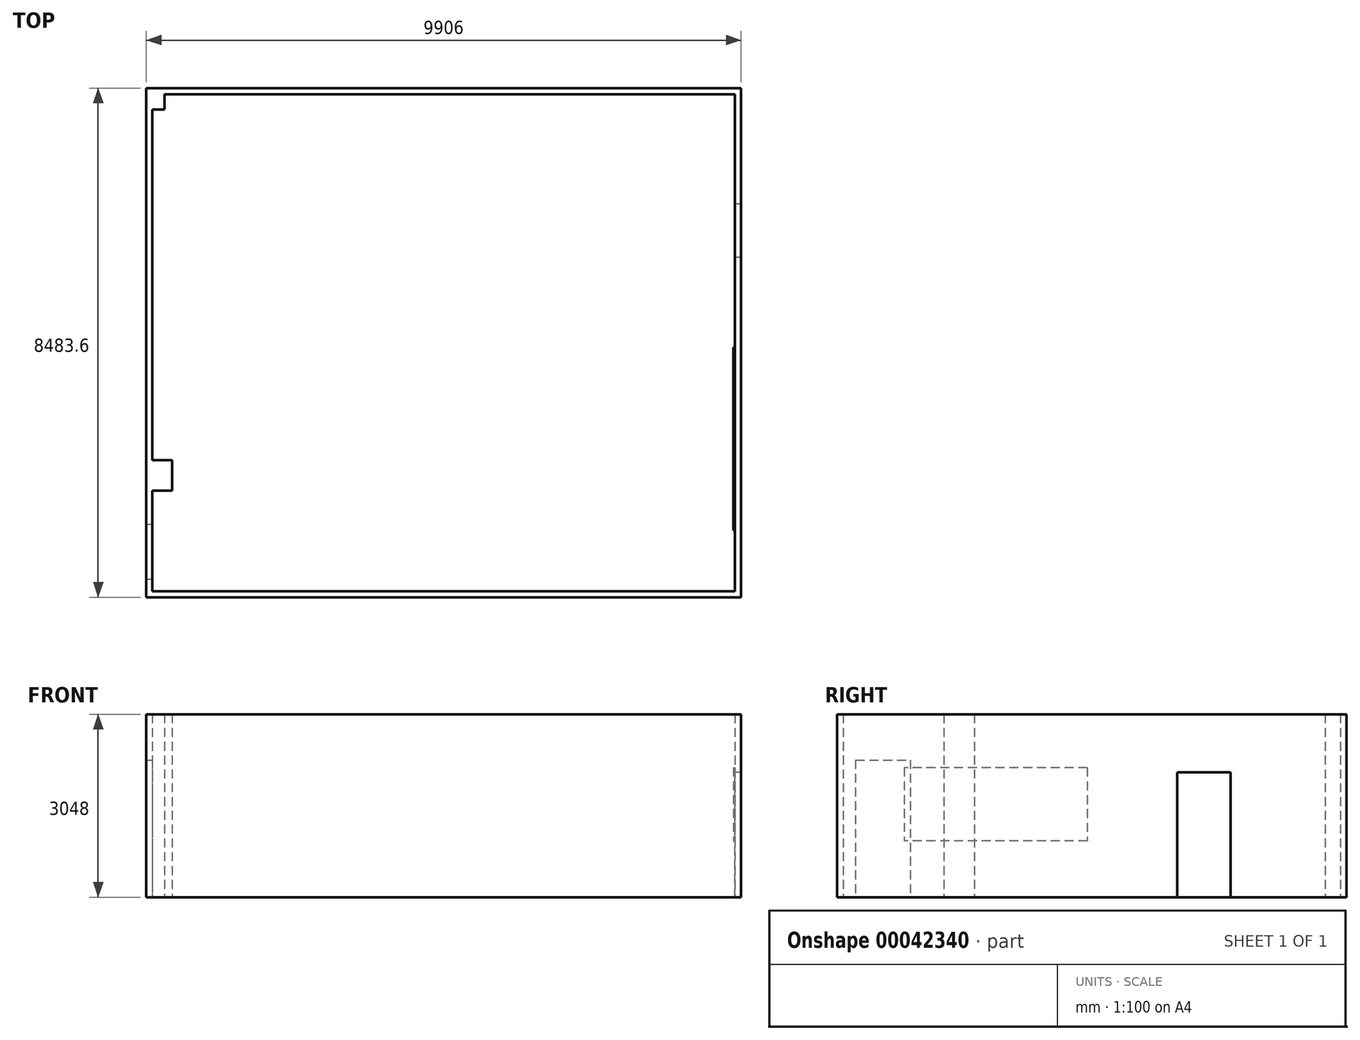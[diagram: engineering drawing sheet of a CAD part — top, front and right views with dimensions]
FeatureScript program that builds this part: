
annotation { "Feature Type Name" : "Feature", "Feature Type Description" : "" }
export const myFeature = defineFeature(function(context is Context, id is Id, definition is map)
    precondition{}
    {
        {
            var Q0;
            Q0=qCreatedBy(makeId("Top.planeOp"),FACE);
            var sketch = newSketch(context, id + "F0", { "sketchPlane" : qUnion([Q0])});
            skLineSegment(sketch, "E0", {"start": v(-4784.19, 3902.48) * mm, "end": v(4918.61, 3902.48) * mm});
            skLineSegment(sketch, "E1", {"start": v(4918.61, 3902.48) * mm, "end": v(4918.61, -4377.92) * mm});
            skLineSegment(sketch, "E2", {"start": v(4918.61, -4377.92) * mm, "end": v(-4784.19, -4377.92) * mm});
            skLineSegment(sketch, "E3", {"start": v(-4784.19, -4377.92) * mm, "end": v(-4784.19, 3902.48) * mm});
            skLineSegment(sketch, "E4.0", {"start": v(-4885.79, -4479.52) * mm, "end": v(-4885.79, 4004.08) * mm});
            skLineSegment(sketch, "E4.1", {"start": v(5020.21, -4479.52) * mm, "end": v(-4885.79, -4479.52) * mm});
            skLineSegment(sketch, "E4.2", {"start": v(5020.21, 4004.08) * mm, "end": v(5020.21, -4479.52) * mm});
            skLineSegment(sketch, "E4.3", {"start": v(-4885.79, 4004.08) * mm, "end": v(5020.21, 4004.08) * mm});
            skSolve(sketch);
        }
        {
            var Q0;
            Q0=makeQuery(id+"F0.imprint","IMPRINT",FACE,{"disambiguationData":[TD([[makeQuery(id+"F0.imprint","IMPRINT",EDGE,{"derivedFrom":sQuery(id+"F0.wireOp",EDGE,"E0")}),1.0]])]});
            extrude(context, id + "F1", {"entities" : qUnion([Q0]), "depth" : 3048 * mm});
        }
        {
            var Q0;
            Q0=makeQuery(id+"F1.opExtrude","SWEPT_FACE",FACE,{"disambiguationData":[OSD([sQuery(id+"F0.wireOp",EDGE,"E1")])]});
            var sketch = newSketch(context, id + "F2", { "sketchPlane" : qUnion([Q0])});
            skSolve(sketch);
        }
        {
            var Q0;
            Q0=makeQuery(id+"F1.opExtrude","SWEPT_FACE",FACE,{"disambiguationData":[OSD([sQuery(id+"F0.wireOp",EDGE,"E0")])]});
            var sketch = newSketch(context, id + "F3", { "sketchPlane" : qUnion([Q0])});
            skSolve(sketch);
        }
        {
            var Q0;
            {var subQ0=sQuery(id+"F0.wireOp",EDGE,"E0");Q0=makeQuery(id+"F3.imprint","IMPRINT",FACE,{"disambiguationData":[TD([[makeQuery(id+"F3.imprint","IMPRINT",EDGE,{"derivedFrom":makeQuery(id+"F1.opExtrude","CAP_EDGE",EDGE,{"disambiguationData":[OSD([subQ0])],"isStart":true})}),1.0]])]});}
            var sketch = newSketch(context, id + "F4", { "sketchPlane" : qUnion([Q0])});
            skLineSegment(sketch, "E5.bottom", {"start": v(-4784.19, 3048) * mm, "end": v(-4580.99, 3048) * mm});
            skLineSegment(sketch, "E5.top", {"start": v(-4784.19, 0) * mm, "end": v(-4580.99, 0) * mm});
            skLineSegment(sketch, "E5.left", {"start": v(-4784.19, 3048) * mm, "end": v(-4784.19, 0) * mm});
            skLineSegment(sketch, "E5.right", {"start": v(-4580.99, 3048) * mm, "end": v(-4580.99, 0) * mm});
            skSolve(sketch);
        }
        {
            var Q0;
            Q0=makeQuery(id+"F4.imprint","IMPRINT",FACE,{"disambiguationData":[TD([[makeQuery(id+"F4.imprint","IMPRINT",EDGE,{"derivedFrom":sQuery(id+"F4.wireOp",EDGE,"E5.bottom")}),-1.0]])]});
            extrude(context, id + "F5", {"entities" : qUnion([Q0]), "operationType" : NewBodyOperationType.ADD, "depth" : 254 * mm});
        }
        {
            var Q0;
            Q0=makeQuery(id+"F1.opExtrude","SWEPT_FACE",FACE,{"disambiguationData":[OSD([sQuery(id+"F0.wireOp",EDGE,"E3")])]});
            var sketch = newSketch(context, id + "F6", { "sketchPlane" : qUnion([Q0])});
            skLineSegment(sketch, "E6.bottom", {"start": v(-4174.72, 2286) * mm, "end": v(-3260.32, 2286) * mm});
            skLineSegment(sketch, "E6.top", {"start": v(-4174.72, 0) * mm, "end": v(-3260.32, 0) * mm});
            skLineSegment(sketch, "E6.left", {"start": v(-4174.72, 2286) * mm, "end": v(-4174.72, 0) * mm});
            skLineSegment(sketch, "E6.right", {"start": v(-3260.32, 2286) * mm, "end": v(-3260.32, 0) * mm});
            skSolve(sketch);
        }
        {
            var Q0;
            Q0=makeQuery(id+"F6.imprint","IMPRINT",FACE,{"disambiguationData":[TD([[makeQuery(id+"F6.imprint","IMPRINT",EDGE,{"derivedFrom":sQuery(id+"F6.wireOp",EDGE,"E6.bottom")}),-1.0]])]});
            extrude(context, id + "F7", {"entities" : qUnion([Q0]), "operationType" : NewBodyOperationType.REMOVE, "endBound" : BoundingType.THROUGH_ALL, "oppositeDirection" : true, "depth" : 25.4 * mm});
        }
        {
            var Q0;
            Q0=makeQuery(id+"F1.opExtrude","SWEPT_FACE",FACE,{"disambiguationData":[OSD([sQuery(id+"F0.wireOp",EDGE,"E3")])]});
            var sketch = newSketch(context, id + "F8", { "sketchPlane" : qUnion([Q0])});
            skLineSegment(sketch, "E7.bottom", {"start": v(-2701.52, 3048) * mm, "end": v(-2193.52, 3048) * mm});
            skLineSegment(sketch, "E7.top", {"start": v(-2701.52, 0) * mm, "end": v(-2193.52, 0) * mm});
            skLineSegment(sketch, "E7.left", {"start": v(-2701.52, 3048) * mm, "end": v(-2701.52, 0) * mm});
            skLineSegment(sketch, "E7.right", {"start": v(-2193.52, 3048) * mm, "end": v(-2193.52, 0) * mm});
            skSolve(sketch);
        }
        {
            var Q0;
            Q0=makeQuery(id+"F8.imprint","IMPRINT",FACE,{"disambiguationData":[TD([[makeQuery(id+"F8.imprint","IMPRINT",EDGE,{"derivedFrom":sQuery(id+"F8.wireOp",EDGE,"E7.bottom")}),-1.0]])]});
            extrude(context, id + "F9", {"entities" : qUnion([Q0]), "operationType" : NewBodyOperationType.ADD, "depth" : 330.2 * mm});
        }
        {
            var Q0;
            {var subQ0=sQuery(id+"F0.wireOp",EDGE,"E1");Q0=makeQuery(id+"F2.imprint","IMPRINT",FACE,{"disambiguationData":[TD([[makeQuery(id+"F2.imprint","IMPRINT",EDGE,{"derivedFrom":makeQuery(id+"F1.opExtrude","CAP_EDGE",EDGE,{"disambiguationData":[OSD([subQ0])],"isStart":true})}),1.0]])]});}
            var sketch = newSketch(context, id + "F10", { "sketchPlane" : qUnion([Q0])});
            skLineSegment(sketch, "E8.bottom", {"start": v(-2073.68, 0) * mm, "end": v(-1184.68, 0) * mm});
            skLineSegment(sketch, "E8.top", {"start": v(-2073.68, 2082.8) * mm, "end": v(-1184.68, 2082.8) * mm});
            skLineSegment(sketch, "E8.left", {"start": v(-2073.68, 0) * mm, "end": v(-2073.68, 2082.8) * mm});
            skLineSegment(sketch, "E8.right", {"start": v(-1184.68, 0) * mm, "end": v(-1184.68, 2082.8) * mm});
            skSolve(sketch);
        }
        {
            var Q0;
            Q0=makeQuery(id+"F10.imprint","IMPRINT",FACE,{"disambiguationData":[TD([[makeQuery(id+"F10.imprint","IMPRINT",EDGE,{"derivedFrom":sQuery(id+"F10.wireOp",EDGE,"E8.bottom")}),1.0]])]});
            extrude(context, id + "F11", {"entities" : qUnion([Q0]), "operationType" : NewBodyOperationType.REMOVE, "endBound" : BoundingType.THROUGH_ALL, "oppositeDirection" : true, "depth" : 25.4 * mm});
        }
        {
            var Q0;
            {var subQ0=sQuery(id+"F0.wireOp",EDGE,"E1");Q0=makeQuery(id+"F2.imprint","IMPRINT",FACE,{"disambiguationData":[TD([[makeQuery(id+"F2.imprint","IMPRINT",EDGE,{"derivedFrom":makeQuery(id+"F1.opExtrude","CAP_EDGE",EDGE,{"disambiguationData":[OSD([subQ0])],"isStart":true})}),1.0]])]});}
            var sketch = newSketch(context, id + "F12", { "sketchPlane" : qUnion([Q0])});
            skLineSegment(sketch, "E9.bottom", {"start": v(313.92, 2159) * mm, "end": v(3361.92, 2159) * mm});
            skLineSegment(sketch, "E9.top", {"start": v(313.92, 939.8) * mm, "end": v(3361.92, 939.8) * mm});
            skLineSegment(sketch, "E9.left", {"start": v(313.92, 2159) * mm, "end": v(313.92, 939.8) * mm});
            skLineSegment(sketch, "E9.right", {"start": v(3361.92, 2159) * mm, "end": v(3361.92, 939.8) * mm});
            skSolve(sketch);
        }
        {
            var Q0;
            Q0=qSketchRegion(id+"F12",true);
            extrude(context, id + "F13", {"entities" : qUnion([Q0]), "depth" : 25.4 * mm});
        }
    });
